# Revit family: LED CUADRATO 01_LZ64P13WW
name_source: partatom
category: Luminarias
units: mm (PartAtom-declared; Revit-internal decimal feet)

## family parameters
Compartido = No
Corte con vacíos al cargar = No
Cota de conector redondo = Diámetro de uso
Origen de luz = Sí
Punto de cálculo de habitación = No
Se basa en plano de trabajo = Sí
Siempre vertical = No
Tipo de pieza = Normal

## types (1)
- LED CUADRATO 01_LZ64P13WW
    Cambio de temperatura de color de luz atenuada = <Ninguno>
    Comentarios de vataje = 90-240V
    Descripción = LUMINARIA DIRIGIBLE TIPO ARBOTANTE, CON ACABADO EN ALUMINIO Y PESO DE 0.48KG, CON UN TIPO DE LED CITIZEN Y UNA POTENCIA DE 4W, 270 LUMENES, TEMPERATURA EN BLANCO CALIDO 3000K, CORRIENTE DE OPERACIÓN 30mA, CABLE DE 8CM, ALIMENTADO A 90-240VAC
    Elevación por defecto = 0 mm  [stored 0 ft]
    Fabricante = BRILLANT
    Filtro de color = 16777215
    Longitud de símbolo de origen de luz = 500 mm  [stored 1.64042 ft]
    Lámpara = CITIZEN
    Modelo = LZ64P13WW
    Watt per fixture = 4
    Ángulo de campo de foco = 90.00°
    Ángulo de enfoque = 30.00°
    Ángulo de inclinación = 90.00°

note: [stored X ft] marks values corroborated as IEEE doubles in the binary element streams (Revit-internal decimal feet)

## geometry (parser evidence)
native form markers: Blend x2
no freeform markers — native parametric forms only
